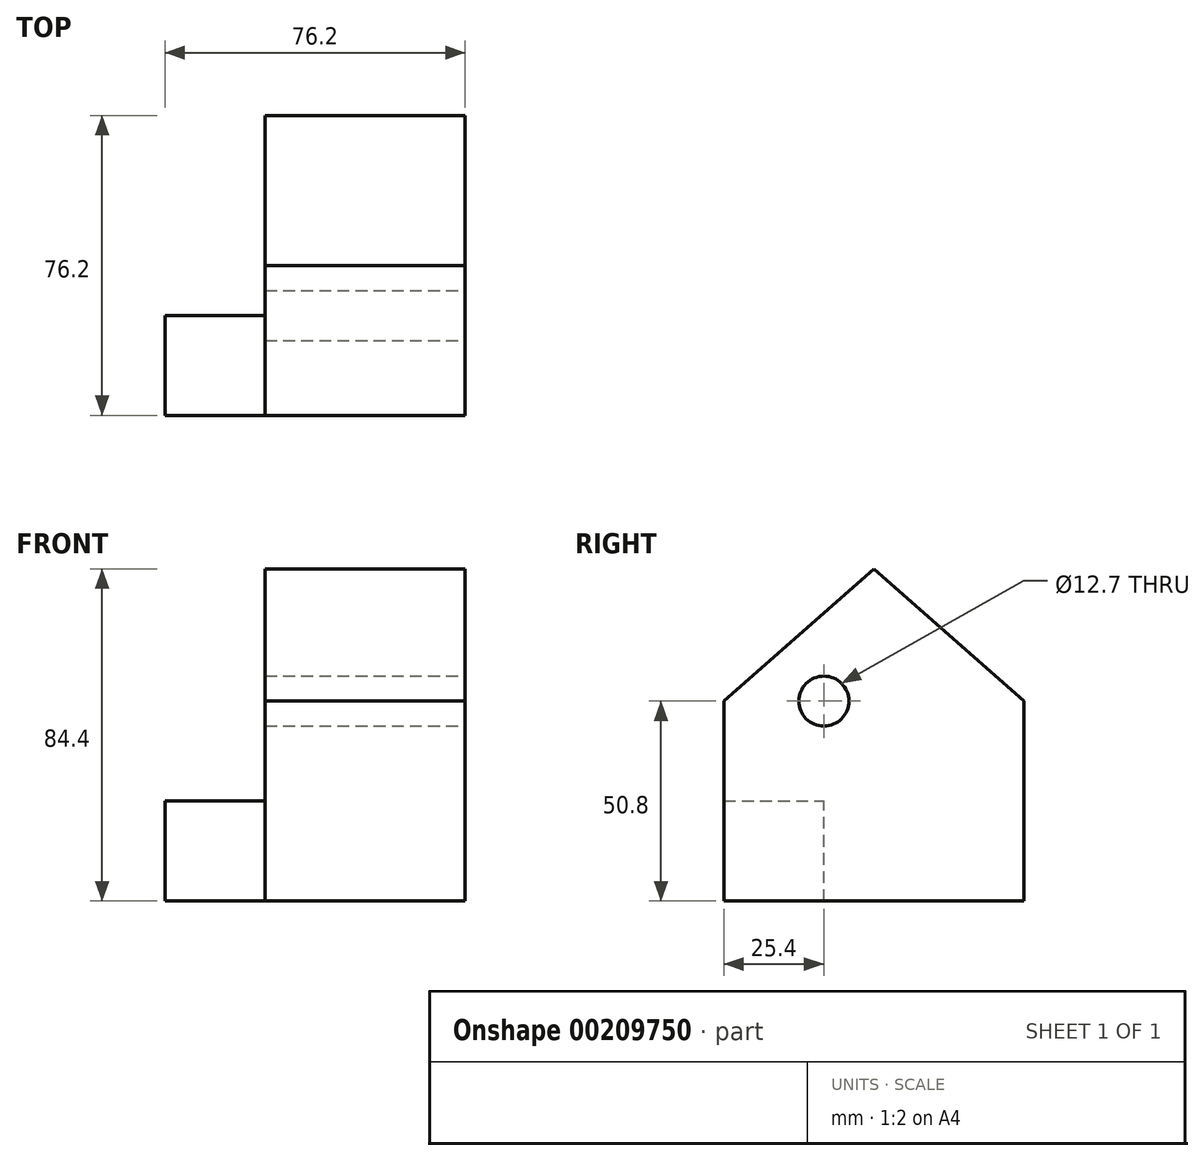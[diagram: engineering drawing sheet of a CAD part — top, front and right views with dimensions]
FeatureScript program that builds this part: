
annotation { "Feature Type Name" : "Feature", "Feature Type Description" : "" }
export const myFeature = defineFeature(function(context is Context, id is Id, definition is map)
    precondition{}
    {
        {
            var Q0;
            Q0=qCreatedBy(makeId("Right.planeOp"),FACE);
            var sketch = newSketch(context, id + "F0", { "sketchPlane" : qUnion([Q0])});
            skLineSegment(sketch, "E0.bottom", {"start": v(0, 0) * mm, "end": v(-76.2, 0) * mm});
            skLineSegment(sketch, "E0.top", {"start": v(0, 50.8) * mm, "end": v(-76.2, 50.8) * mm});
            skLineSegment(sketch, "E0.left", {"start": v(0, 0) * mm, "end": v(0, 50.8) * mm});
            skLineSegment(sketch, "E0.right", {"start": v(-76.2, 0) * mm, "end": v(-76.2, 50.8) * mm});
            skLineSegment(sketch, "E1", {"start": v(0, 50.8) * mm, "end": v(-38.1, 84.4) * mm});
            skLineSegment(sketch, "E2", {"start": v(-38.1, 84.4) * mm, "end": v(-76.2, 50.8) * mm});
            skSolve(sketch);
        }
        {
            var Q0;
            Q0 = qSketchRegion(id + "F0", true);
            extrude(context, id + "F1", {"entities" : qUnion([Q0]), "depth" : 50.8 * mm});
        }
        {
            var Q0;
            Q0=makeQuery(id+"F1.opExtrude","CAP_FACE",FACE,{"disambiguationData":[OSD([sQuery(id+"F0.wireOp",EDGE,"E0.bottom"),sQuery(id+"F0.wireOp",EDGE,"E0.left"),sQuery(id+"F0.wireOp",EDGE,"E0.right"),sQuery(id+"F0.wireOp",EDGE,"E1"),sQuery(id+"F0.wireOp",EDGE,"E2")])],"isStart":false});
            var sketch = newSketch(context, id + "F2", { "sketchPlane" : qUnion([Q0])});
            skCircle(sketch, "E3", {"center": v(-50.8, 50.8) * mm, "radius": 6.35 * mm});
            skSolve(sketch);
        }
        {
            var Q0;
            Q0 = qSketchRegion(id + "F2", true);
            extrude(context, id + "F3", {"entities" : qUnion([Q0]), "operationType" : NewBodyOperationType.REMOVE, "endBound" : BoundingType.THROUGH_ALL, "oppositeDirection" : true, "depth" : 25.4 * mm});
        }
        {
            var Q0;
            Q0=qCreatedBy(makeId("Right.planeOp"),FACE);
            var sketch = newSketch(context, id + "F4", { "sketchPlane" : qUnion([Q0])});
            skFitSpline(sketch, "E4", {"points": [v(39.22, 36.95) * mm, v(46.72, 44.45) * mm, v(55.02, 37.48) * mm, v(44.04, 35.88) * mm, v(48.33, 38.82) * mm, v(43.24, 40.16) * mm, v(39.22, 36.95) * mm]});
            skSolve(sketch);
        }
        {
            var Q0;
            Q0 = qSketchRegion(id + "F4", true);
            extrude(context, id + "F5", {"entities" : qUnion([Q0]), "operationType" : NewBodyOperationType.REMOVE, "endBound" : BoundingType.THROUGH_ALL, "oppositeDirection" : true, "depth" : 25.4 * mm});
        }
        {
            var Q0;
            Q0=makeQuery(id+"F1.opExtrude","CAP_FACE",FACE,{"disambiguationData":[OSD([sQuery(id+"F0.wireOp",EDGE,"E0.bottom"),sQuery(id+"F0.wireOp",EDGE,"E0.left"),sQuery(id+"F0.wireOp",EDGE,"E0.right"),sQuery(id+"F0.wireOp",EDGE,"E1"),sQuery(id+"F0.wireOp",EDGE,"E2")])],"isStart":true});
            var sketch = newSketch(context, id + "F6", { "sketchPlane" : qUnion([Q0])});
            skLineSegment(sketch, "E5.bottom", {"start": v(76.2, 0) * mm, "end": v(50.8, 0) * mm});
            skLineSegment(sketch, "E5.top", {"start": v(76.2, 25.4) * mm, "end": v(50.8, 25.4) * mm});
            skLineSegment(sketch, "E5.left", {"start": v(76.2, 0) * mm, "end": v(76.2, 25.4) * mm});
            skLineSegment(sketch, "E5.right", {"start": v(50.8, 0) * mm, "end": v(50.8, 25.4) * mm});
            skSolve(sketch);
        }
        {
            var Q0;
            Q0=makeQuery(id+"F6.imprint","IMPRINT",FACE,{"disambiguationData":[TD([[makeQuery(id+"F6.imprint","IMPRINT",EDGE,{"derivedFrom":sQuery(id+"F6.wireOp",EDGE,"E5.bottom")}),1.0]])]});
            extrude(context, id + "F7", {"entities" : qUnion([Q0]), "depth" : 25.4 * mm});
        }
    });
